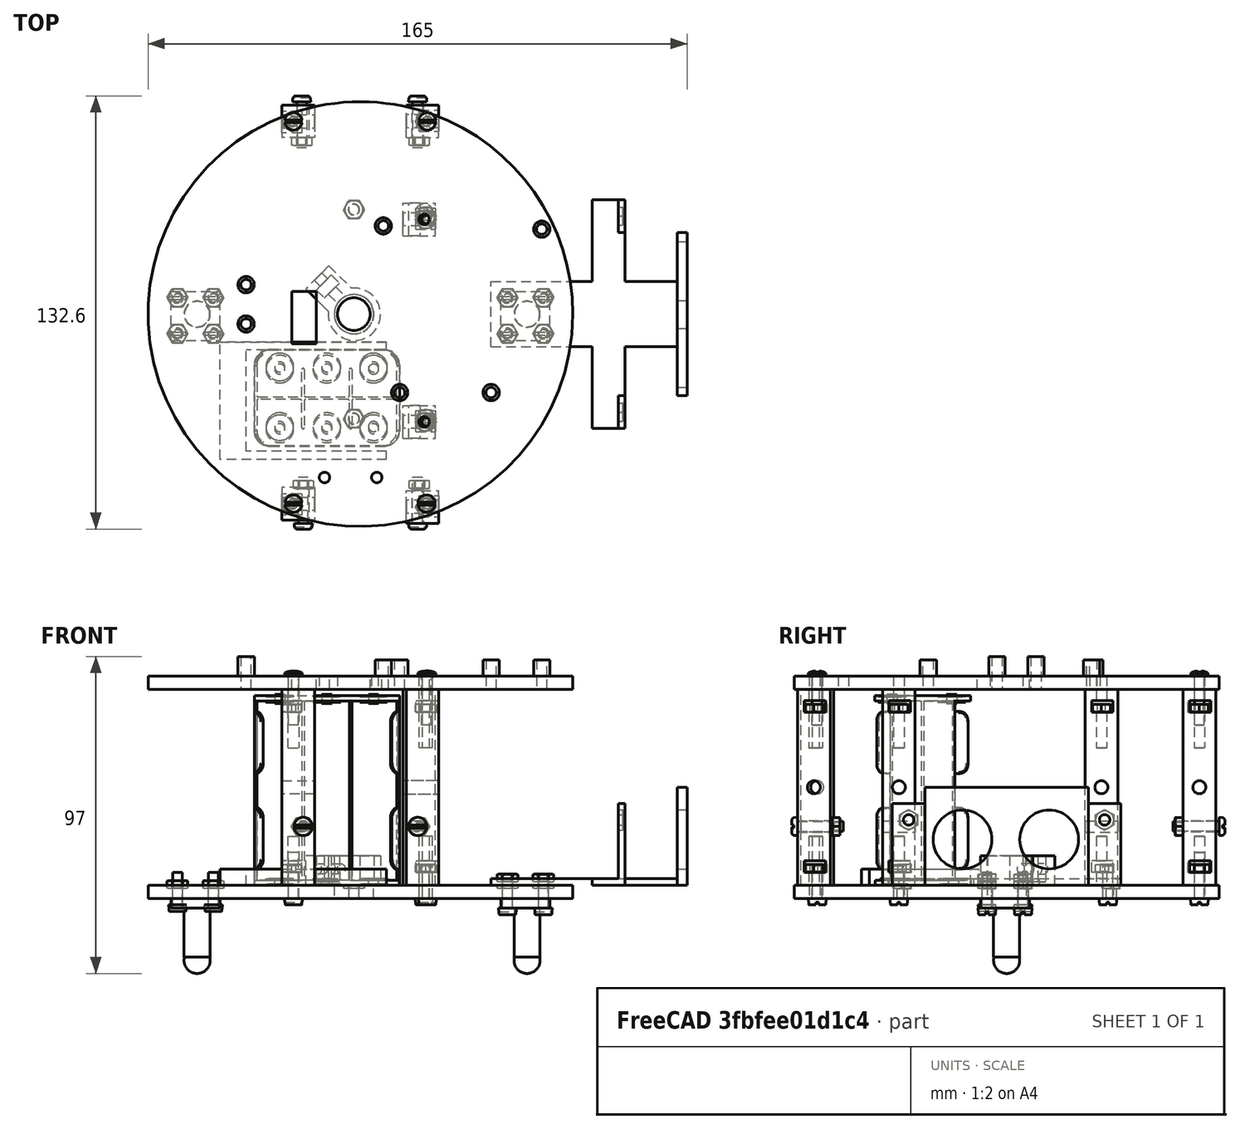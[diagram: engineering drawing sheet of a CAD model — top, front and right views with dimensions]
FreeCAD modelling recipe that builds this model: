
FCSTD DOCUMENT  (FreeCAD 0.21R33668 +26 (Git))
Label: ANIMAMOTORES
License: All rights reserved
LicenseURL: https://en.wikipedia.org/wiki/All_rights_reserved
objects: Part::FeaturePython×46, App::DocumentObjectGroupPython×21, Part::MultiFuse×14, Part::Feature×12, Mesh::Feature×2
note: 72 computed .brp shape members not serialized (recipe doc carries the construction recipe); baked Part::Feature solids carry a one-line shape summary decoded from their .brp

FEATURE [Part::Feature] Cut009_solid  label="ballCSensor"
  Placement = pos=(0,0,20) rot=(0,0,1;0rad)
  shape: bbox 15 x 15 x 23 mm, 13 faces (baked)
FEATURE [Part::Feature] Fusion060_solid  label="plataformaInferior (Solid)"
  Placement = pos=(0,0,20) rot=(0,0,1;0rad)
  shape: bbox 130 x 130 x 13 mm, 195 faces (baked)
FEATURE [Part::FeaturePython] Nut  label="M3-Tuerca"  # Fasteners workbench fastener (typed FeaturePython)
  Placement = pos=(41,5,8) rot=(0,0,1;0rad)
  diameter = 4
  invert = false
  leftHanded = false
  matchOuter = false
  offset = 0
  thread = false
  type = 22
FEATURE [Part::FeaturePython] Nut001  label="M3-Tuerca004"  # Fasteners workbench fastener (typed FeaturePython)
  Placement = pos=(52,5,8) rot=(0,0,1;0rad)
  diameter = 4
  invert = false
  leftHanded = false
  matchOuter = false
  offset = 0
  thread = false
  type = 22
FEATURE [Part::FeaturePython] Nut002  label="M3-Tuerca006"  # Fasteners workbench fastener (typed FeaturePython)
  Placement = pos=(52,-6,8) rot=(0,0,1;0rad)
  diameter = 4
  invert = false
  leftHanded = false
  matchOuter = false
  offset = 0
  thread = false
  type = 22
FEATURE [Part::FeaturePython] Nut003  label="M3-Tuerca005"  # Fasteners workbench fastener (typed FeaturePython)
  Placement = pos=(41,-6,8) rot=(0,0,1;0rad)
  diameter = 4
  invert = false
  leftHanded = false
  matchOuter = false
  offset = 0
  thread = false
  type = 22
FEATURE [Part::MultiFuse] Fusion  label="tuercasBallCSensor"
  Placement = pos=(0,0,2) rot=(0,0,1;0rad)
  Shapes = -> [Nut,Nut001,Nut002,Nut003]
FEATURE [Part::FeaturePython] Nut004  label="M3-Tuerca007"  # Fasteners workbench fastener (typed FeaturePython)
  Placement = pos=(41,5,8) rot=(0,0,1;0rad)
  diameter = 4
  invert = false
  leftHanded = false
  matchOuter = false
  offset = 0
  thread = false
  type = 22
FEATURE [Part::FeaturePython] Nut005  label="M3-Tuerca008"  # Fasteners workbench fastener (typed FeaturePython)
  Placement = pos=(52,5,8) rot=(0,0,1;0rad)
  diameter = 4
  invert = false
  leftHanded = false
  matchOuter = false
  offset = 0
  thread = false
  type = 22
FEATURE [Part::FeaturePython] Nut006  label="M3-Tuerca009"  # Fasteners workbench fastener (typed FeaturePython)
  Placement = pos=(52,-6,8) rot=(0,0,1;0rad)
  diameter = 4
  invert = false
  leftHanded = false
  matchOuter = false
  offset = 0
  thread = false
  type = 22
FEATURE [Part::FeaturePython] Nut007  label="M3-Tuerca010"  # Fasteners workbench fastener (typed FeaturePython)
  Placement = pos=(41,-6,8) rot=(0,0,1;0rad)
  diameter = 4
  invert = false
  leftHanded = false
  matchOuter = false
  offset = 0
  thread = false
  type = 22
FEATURE [Part::MultiFuse] Fusion001  label="tuercasBallCLibre"
  Placement = pos=(-101,0,0) rot=(0,0,1;0rad)
  Shapes = -> [Nut004,Nut005,Nut006,Nut007]
FEATURE [Part::Feature] Cut009_solid001  label="ballCLibre"
  Placement = pos=(-101,0,20) rot=(0,0,1;0rad)
  shape: bbox 15 x 15 x 23 mm, 13 faces (baked)
FEATURE [Part::Feature] Cut_solid  label="soporteSensores (Solid)"
  Placement = pos=(15,0,20) rot=(0,0,1;0rad)
  shape: bbox 60 x 70 x 30 mm, 144 faces (baked)
FEATURE [Part::FeaturePython] Screw  label="M3x10-Tornillo"  # Fasteners workbench fastener (typed FeaturePython)
  Placement = pos=(-60,5,3) rot=(1,0,0;3.14159rad)
  diameter = 4
  invert = false
  leftHanded = false
  length = 4
  lengthCustom = 10
  matchOuter = false
  offset = 0
  thread = false
  type = 30
FEATURE [Part::FeaturePython] Screw001  label="M3x10-Tornillo001"  # Fasteners workbench fastener (typed FeaturePython)
  Placement = pos=(-60,-6,3) rot=(1,0,0;3.14159rad)
  diameter = 4
  invert = false
  leftHanded = false
  length = 4
  lengthCustom = 10
  matchOuter = false
  offset = 0
  thread = false
  type = 30
FEATURE [Part::FeaturePython] Screw002  label="M3x10-Tornillo002"  # Fasteners workbench fastener (typed FeaturePython)
  Placement = pos=(-49,-6,3) rot=(1,0,0;3.14159rad)
  diameter = 4
  invert = false
  leftHanded = false
  length = 4
  lengthCustom = 10
  matchOuter = false
  offset = 0
  thread = false
  type = 30
FEATURE [Part::FeaturePython] Screw003  label="M3x10-Tornillo003"  # Fasteners workbench fastener (typed FeaturePython)
  Placement = pos=(-49,5,3) rot=(1,0,0;3.14159rad)
  diameter = 4
  invert = false
  leftHanded = false
  length = 4
  lengthCustom = 10
  matchOuter = false
  offset = 0
  thread = false
  type = 30
FEATURE [Part::MultiFuse] Fusion002  label="tornillosBallClibre"
  Shapes = -> [Screw,Screw001,Screw002,Screw003]
FEATURE [Part::FeaturePython] Screw004  label="M3x10-Tornillo004"  # Fasteners workbench fastener (typed FeaturePython)
  Placement = pos=(-60,5,3) rot=(1,0,0;3.14159rad)
  diameter = 4
  invert = false
  leftHanded = false
  length = 4
  lengthCustom = 10
  matchOuter = false
  offset = 0
  thread = false
  type = 30
FEATURE [Part::FeaturePython] Screw005  label="M3x10-Tornillo005"  # Fasteners workbench fastener (typed FeaturePython)
  Placement = pos=(-60,-6,3) rot=(1,0,0;3.14159rad)
  diameter = 4
  invert = false
  leftHanded = false
  length = 4
  lengthCustom = 10
  matchOuter = false
  offset = 0
  thread = false
  type = 30
FEATURE [Part::FeaturePython] Screw006  label="M3x10-Tornillo006"  # Fasteners workbench fastener (typed FeaturePython)
  Placement = pos=(-49,-6,3) rot=(1,0,0;3.14159rad)
  diameter = 4
  invert = false
  leftHanded = false
  length = 4
  lengthCustom = 10
  matchOuter = false
  offset = 0
  thread = false
  type = 30
FEATURE [Part::FeaturePython] Screw007  label="M3x10-Tornillo007"  # Fasteners workbench fastener (typed FeaturePython)
  Placement = pos=(-49,5,3) rot=(1,0,0;3.14159rad)
  diameter = 4
  invert = false
  leftHanded = false
  length = 4
  lengthCustom = 10
  matchOuter = false
  offset = 0
  thread = false
  type = 30
FEATURE [Part::MultiFuse] Fusion003  label="tornillosBallCSensor"
  Placement = pos=(101,0,-1) rot=(0,0,1;0rad)
  Shapes = -> [Screw004,Screw005,Screw006,Screw007]
FEATURE [App::DocumentObjectGroupPython] SimpleGroup  # scripted group (container) (typed FeaturePython)
  AnimationStepTime = 0
  AnimationSteps = 20
  Distance = 19
  Revolutions = 0
  dir_vectors = (1) [(0,0,1)]
  rot_centers = (1) [(-54.5,-0.5,-14)]
  rot_vectors = (1) [(0,0,1)]
FEATURE [App::DocumentObjectGroupPython] SimpleGroup003  # scripted group (container) (typed FeaturePython)
  AnimationStepTime = 0
  AnimationSteps = 20
  Distance = 20
  Revolutions = 0
  dir_vectors = (1) [(0,0,-1)]
  rot_centers = (1) [(-60,-6,26)]
  rot_vectors = (1) [(0,0,-1)]
FEATURE [App::DocumentObjectGroupPython] SimpleGroup004  # scripted group (container) (typed FeaturePython)
  AnimationStepTime = 0
  AnimationSteps = 20
  Distance = 40
  Revolutions = 0
  dir_vectors = (1) [(0,1.22465e-16,1)]
  rot_centers = (1) [(-60,5,-27)]
  rot_vectors = (1) [(0,1.22465e-16,1)]
FEATURE [App::DocumentObjectGroupPython] SimpleGroup005  # scripted group (container) (typed FeaturePython)
  AnimationStepTime = 0
  AnimationSteps = 20
  Distance = 19
  Revolutions = 0
  dir_vectors = (1) [(0,0,1)]
  rot_centers = (1) [(46.5,-0.5,-14)]
  rot_vectors = (1) [(0,0,1)]
FEATURE [Part::Feature] Part__Feature  label="6 x AAA Holder"
  Placement = pos=(-100,212,67) rot=(0.57735,0.57735,-0.57735;2.0944rad)
  shape: bbox 45.01 x 29.59 x 58.41 mm, 300 faces, 8 solids (baked)
FEATURE [App::DocumentObjectGroupPython] SimpleGroup006  # scripted group (container) (typed FeaturePython)
  AnimationStepTime = 0
  AnimationSteps = 20
  Distance = 100
  Revolutions = 0
  dir_vectors = (1) [(-1,-6.69631e-16,-2.22045e-16)]
  rot_centers = (1) [(13.5,-25.9132,38.8088)]
  rot_vectors = (1) [(-1,-6.69631e-16,-2.22045e-16)]
FEATURE [App::DocumentObjectGroupPython] SimpleGroup007  # scripted group (container) (typed FeaturePython)
  AnimationStepTime = 0
  AnimationSteps = 20
  Distance = 15
  Revolutions = 0
  dir_vectors = (1) [(0,0,-1)]
  rot_centers = (1) [(72,-3.55271e-16,24)]
  rot_vectors = (1) [(0,0,-1)]
FEATURE [App::DocumentObjectGroupPython] SimpleGroup008  # scripted group (container) (typed FeaturePython)
  AnimationStepTime = 0
  AnimationSteps = 20
  Distance = 18
  Revolutions = 0
  dir_vectors = (1) [(0,0,-1)]
  rot_centers = (1) [(52,-6,28)]
  rot_vectors = (1) [(0,0,-1)]
FEATURE [App::DocumentObjectGroupPython] SimpleGroup009  # scripted group (container) (typed FeaturePython)
  AnimationStepTime = 0
  AnimationSteps = 20
  Distance = 39
  Revolutions = 0
  dir_vectors = (1) [(0,0,1)]
  rot_centers = (1) [(52,-6,-27)]
  rot_vectors = (1) [(0,0,1)]
FEATURE [Part::Feature] Cut_solid006  label="columna (Solid)004"
  Placement = pos=(0,-21,0) rot=(0,0,1;0rad)
  shape: bbox 10 x 10 x 60 mm, 24 faces (baked)
FEATURE [Part::Feature] Cut_solid004  label="columna (Solid)002"
  Placement = pos=(-8,21,0) rot=(0,0,1;3.14159rad)
  shape: bbox 10 x 10 x 60 mm, 24 faces (baked)
FEATURE [Part::Feature] Cut_solid007  label="columna (Solid)005"
  Placement = pos=(-8,-96,0) rot=(0,0,1;3.14159rad)
  shape: bbox 10 x 10 x 60 mm, 24 faces (baked)
FEATURE [Part::Feature] Cut_solid003  label="columna (Solid)001"
  Placement = pos=(-1,67,0) rot=(0,0,1;0rad)
  shape: bbox 10 x 10 x 60 mm, 24 faces (baked)
FEATURE [Part::Feature] Cut_solid005  label="columna (Solid)003"
  Placement = pos=(0,97,0) rot=(0,0,1;0rad)
  shape: bbox 10 x 10 x 60 mm, 24 faces (baked)
FEATURE [Part::FeaturePython] Screw008  label="M3x10-Tornillo008"  # Fasteners workbench fastener (typed FeaturePython)
  Placement = pos=(-24.5,-58,5) rot=(1,0,0;3.14159rad)
  diameter = 4
  invert = false
  leftHanded = false
  length = 4
  lengthCustom = 10
  matchOuter = false
  offset = 0
  thread = false
  type = 30
FEATURE [Part::FeaturePython] Screw009  label="M3x10-Tornillo009"  # Fasteners workbench fastener (typed FeaturePython)
  Placement = pos=(16.5,-58,5) rot=(1,0,0;3.14159rad)
  diameter = 4
  invert = false
  leftHanded = false
  length = 4
  lengthCustom = 10
  matchOuter = false
  offset = 0
  thread = false
  type = 30
FEATURE [Part::FeaturePython] Screw010  label="M3x10-Tornillo010"  # Fasteners workbench fastener (typed FeaturePython)
  Placement = pos=(15.5,-33,5) rot=(1,0,0;3.14159rad)
  diameter = 4
  invert = false
  leftHanded = false
  length = 4
  lengthCustom = 10
  matchOuter = false
  offset = 0
  thread = false
  type = 30
FEATURE [Part::FeaturePython] Screw011  label="M3x10-Tornillo011"  # Fasteners workbench fastener (typed FeaturePython)
  Placement = pos=(15.5,31,5) rot=(1,0,0;3.14159rad)
  diameter = 4
  invert = false
  leftHanded = false
  length = 4
  lengthCustom = 10
  matchOuter = false
  offset = 0
  thread = false
  type = 30
FEATURE [Part::FeaturePython] Screw012  label="M3x10-Tornillo012"  # Fasteners workbench fastener (typed FeaturePython)
  Placement = pos=(16.5,59,5) rot=(1,0,0;3.14159rad)
  diameter = 4
  invert = false
  leftHanded = false
  length = 4
  lengthCustom = 10
  matchOuter = false
  offset = 0
  thread = false
  type = 30
FEATURE [Part::FeaturePython] Screw013  label="M3x14-Tornillo"  # Fasteners workbench fastener (typed FeaturePython)
  Placement = pos=(-24.5,59,5) rot=(1,0,0;3.14159rad)
  diameter = 4
  invert = false
  leftHanded = false
  length = 6
  lengthCustom = 14
  matchOuter = false
  offset = 0
  thread = false
  type = 30
FEATURE [Part::Feature] Cut_solid002  label="columna (Solid)"
  Placement = pos=(-1,5,0) rot=(0,0,1;0rad)
  shape: bbox 10 x 10 x 60 mm, 24 faces (baked)
FEATURE [Part::MultiFuse] Fusion004  label="columnas"
  Placement = pos=(0,0,20) rot=(0,0,1;0rad)
  Shapes = -> [Cut_solid006,Cut_solid004,Cut_solid007,Cut_solid003,Cut_solid005,Cut_solid002]
FEATURE [Part::MultiFuse] Fusion005  label="tornillosAbajo"
  Shapes = -> [Screw008,Screw009,Screw010,Screw011,Screw012,Screw013]
FEATURE [Part::FeaturePython] Nut008  label="M3-Tuerca011"  # Fasteners workbench fastener (typed FeaturePython)
  Placement = pos=(16,30,23) rot=(0,0,1;0rad)
  diameter = 4
  invert = false
  leftHanded = false
  matchOuter = false
  offset = 0
  thread = false
  type = 22
FEATURE [Part::FeaturePython] Nut009  label="M3-Tuerca012"  # Fasteners workbench fastener (typed FeaturePython)
  Placement = pos=(16,-32,23) rot=(0,0,1;0rad)
  diameter = 4
  invert = false
  leftHanded = false
  matchOuter = false
  offset = 0
  thread = false
  type = 22
FEATURE [Part::FeaturePython] Nut010  label="M3-Tuerca013"  # Fasteners workbench fastener (typed FeaturePython)
  Placement = pos=(16,-59,23) rot=(0,0,1;0rad)
  diameter = 4
  invert = false
  leftHanded = false
  matchOuter = false
  offset = 0
  thread = false
  type = 22
FEATURE [Part::FeaturePython] Nut011  label="M3-Tuerca014"  # Fasteners workbench fastener (typed FeaturePython)
  Placement = pos=(16,-59,72) rot=(0,0,1;0rad)
  diameter = 4
  invert = false
  leftHanded = false
  matchOuter = false
  offset = 0
  thread = false
  type = 22
FEATURE [Part::FeaturePython] Nut012  label="M3-Tuerca015"  # Fasteners workbench fastener (typed FeaturePython)
  Placement = pos=(16,-33,72) rot=(0,0,1;0rad)
  diameter = 4
  invert = false
  leftHanded = false
  matchOuter = false
  offset = 0
  thread = false
  type = 22
FEATURE [Part::FeaturePython] Nut013  label="M3-Tuerca016"  # Fasteners workbench fastener (typed FeaturePython)
  Placement = pos=(16,29,72) rot=(0,0,1;0rad)
  diameter = 4
  invert = false
  leftHanded = false
  matchOuter = false
  offset = 0
  thread = false
  type = 22
FEATURE [Part::FeaturePython] Nut014  label="M3-Tuerca017"  # Fasteners workbench fastener (typed FeaturePython)
  Placement = pos=(16,59,72) rot=(0,0,1;0rad)
  diameter = 4
  invert = false
  leftHanded = false
  matchOuter = false
  offset = 0
  thread = false
  type = 22
FEATURE [Part::FeaturePython] Nut015  label="M3-Tuerca018"  # Fasteners workbench fastener (typed FeaturePython)
  Placement = pos=(16,59,23) rot=(0,0,1;0.523599rad)
  diameter = 4
  invert = false
  leftHanded = false
  matchOuter = false
  offset = 0
  thread = false
  type = 22
FEATURE [Part::MultiFuse] Fusion006  label="tuercasDelante"
  Placement = pos=(0,0,-10) rot=(0,0,1;0rad)
  Shapes = -> [Nut015,Nut008,Nut009,Nut010,Nut011,Nut012,Nut013,Nut014]
FEATURE [App::DocumentObjectGroupPython] SimpleGroup010  # scripted group (container) (typed FeaturePython)
  AnimationStepTime = 0
  AnimationSteps = 20
  Distance = 20
  Revolutions = 0
  dir_vectors = (1) [(-1,5.55112e-16,0)]
  rot_centers = (1) [(38.25,59,24.2)]
  rot_vectors = (1) [(-1,5.55112e-16,0)]
FEATURE [Part::FeaturePython] Nut016  label="M3-Tuerca021"  # Fasteners workbench fastener (typed FeaturePython)
  Placement = pos=(-25,59,23) rot=(0,0,1;0.523599rad)
  diameter = 4
  invert = false
  leftHanded = false
  matchOuter = false
  offset = 0
  thread = false
  type = 22
FEATURE [Part::FeaturePython] Nut017  label="M3-Tuerca022"  # Fasteners workbench fastener (typed FeaturePython)
  Placement = pos=(-25,59,72) rot=(0,0,1;0.523599rad)
  diameter = 4
  invert = false
  leftHanded = false
  matchOuter = false
  offset = 0
  thread = false
  type = 22
FEATURE [Part::FeaturePython] Nut018  label="M3-Tuerca023"  # Fasteners workbench fastener (typed FeaturePython)
  Placement = pos=(-25,-58,72) rot=(0,0,1;0.523599rad)
  diameter = 4
  invert = false
  leftHanded = false
  matchOuter = false
  offset = 0
  thread = false
  type = 22
FEATURE [Part::FeaturePython] Nut019  label="M3-Tuerca024"  # Fasteners workbench fastener (typed FeaturePython)
  Placement = pos=(-25,-58,23) rot=(0,0,1;0.523599rad)
  diameter = 4
  invert = false
  leftHanded = false
  matchOuter = false
  offset = 0
  thread = false
  type = 22
FEATURE [Part::MultiFuse] Fusion007  label="tuercasAtras"
  Placement = pos=(0,0,-10) rot=(0,0,1;0rad)
  Shapes = -> [Nut019,Nut016,Nut017,Nut018]
FEATURE [App::DocumentObjectGroupPython] SimpleGroup011  # scripted group (container) (typed FeaturePython)
  AnimationStepTime = 0
  AnimationSteps = 20
  Distance = 20
  Revolutions = 0
  dir_vectors = (1) [(1,-1.66533e-16,0)]
  rot_centers = (1) [(-42.25,-58,73.2)]
  rot_vectors = (1) [(1,-1.66533e-16,0)]
FEATURE [App::DocumentObjectGroupPython] SimpleGroup012  # scripted group (container) (typed FeaturePython)
  AnimationStepTime = 0
  AnimationSteps = 20
  Distance = -10
  Revolutions = 0
  dir_vectors = (3) [(0,0,1),(0,0,1),(0,0,1)]
  rot_centers = (3) [(-2.75414,1.04693,9),(-2.75414,1.04693,9),(-2.75414,1.04693,9)]
  rot_vectors = (3) [(0,0,1),(0,0,1),(0,0,1)]
FEATURE [App::DocumentObjectGroupPython] SimpleGroup013  # scripted group (container) (typed FeaturePython)
  AnimationStepTime = 0
  AnimationSteps = 20
  Distance = -20
  Revolutions = 0
  dir_vectors = (1) [(0,0,-1)]
  rot_centers = (1) [(-4.00424,0.00296236,5)]
  rot_vectors = (1) [(0,0,-1)]
FEATURE [Mesh::Feature] _8BYJ_48_v007  label="28BYJ-48_v007"
  Placement = pos=(-8.5,-31,24.5) rot=(0,0,1;3.14159rad)
FEATURE [Mesh::Feature] _8BYJ_48_v6  label="28BYJ-48_v6"
  Placement = pos=(0.5,32,25) rot=(0,0,1;0rad)
FEATURE [Part::FeaturePython] Screw014  label="M3x14-Tornillo006"  # Fasteners workbench fastener (typed FeaturePython)
  Placement = pos=(-21.5,-64,27) rot=(1,0,0;1.5708rad)
  diameter = 4
  invert = false
  leftHanded = false
  length = 5
  lengthCustom = 14
  matchOuter = false
  offset = 0
  thread = false
  type = 36
FEATURE [Part::FeaturePython] Screw015  label="M3x14-Tornillo007"  # Fasteners workbench fastener (typed FeaturePython)
  Placement = pos=(13.5,-64,27) rot=(1,0,0;1.5708rad)
  diameter = 4
  invert = false
  leftHanded = false
  length = 5
  lengthCustom = 14
  matchOuter = false
  offset = 0
  thread = false
  type = 36
FEATURE [Part::FeaturePython] Screw016  label="M3x14-Tornillo005"  # Fasteners workbench fastener (typed FeaturePython)
  Placement = pos=(13.5,65,27) rot=(0,0.707107,0.707107;3.14159rad)
  diameter = 4
  invert = false
  leftHanded = false
  length = 5
  lengthCustom = 14
  matchOuter = false
  offset = 0
  thread = false
  type = 36
FEATURE [Part::FeaturePython] Screw017  label="M3x14-Tornillo004"  # Fasteners workbench fastener (typed FeaturePython)
  Placement = pos=(-22,65,27) rot=(0,0.707107,0.707107;3.14159rad)
  diameter = 4
  invert = false
  leftHanded = false
  length = 5
  lengthCustom = 14
  matchOuter = false
  offset = 0
  thread = false
  type = 36
FEATURE [Part::FeaturePython] Nut020  label="M3-Tuerca025"  # Fasteners workbench fastener (typed FeaturePython)
  Placement = pos=(-22,54,27) rot=(1,0,0;1.5708rad)
  diameter = 4
  invert = false
  leftHanded = false
  matchOuter = false
  offset = 0
  thread = false
  type = 22
FEATURE [Part::FeaturePython] Nut021  label="M3-Tuerca026"  # Fasteners workbench fastener (typed FeaturePython)
  Placement = pos=(14,54,27) rot=(1,0,0;1.5708rad)
  diameter = 4
  invert = false
  leftHanded = false
  matchOuter = false
  offset = 0
  thread = false
  type = 22
FEATURE [Part::FeaturePython] Nut022  label="M3-Tuerca027"  # Fasteners workbench fastener (typed FeaturePython)
  Placement = pos=(14,-51,27) rot=(1,0,0;1.5708rad)
  diameter = 4
  invert = false
  leftHanded = false
  matchOuter = false
  offset = 0
  thread = false
  type = 22
FEATURE [Part::FeaturePython] Nut023  label="M3-Tuerca028"  # Fasteners workbench fastener (typed FeaturePython)
  Placement = pos=(-21.5,-51,27) rot=(1,0,0;1.5708rad)
  diameter = 4
  invert = false
  leftHanded = false
  matchOuter = false
  offset = 0
  thread = false
  type = 22
FEATURE [Part::MultiFuse] Fusion008  label="tornillosDerecha"
  Shapes = -> [Screw014,Screw015]
FEATURE [Part::MultiFuse] Fusion009  label="tuercasDerecha"
  Shapes = -> [Nut022,Nut023]
FEATURE [App::DocumentObjectGroupPython] SimpleGroup014  # scripted group (container) (typed FeaturePython)
  AnimationStepTime = 0
  AnimationSteps = 20
  Distance = -20
  Revolutions = 0
  dir_vectors = (1) [(0,-1,0)]
  rot_centers = (1) [(-23.023,-63,39.1844)]
  rot_vectors = (1) [(0,-1,0)]
FEATURE [App::DocumentObjectGroupPython] SimpleGroup015  # scripted group (container) (typed FeaturePython)
  AnimationStepTime = 0
  AnimationSteps = 20
  Distance = -40
  Revolutions = 0
  dir_vectors = (1) [(0,-1,0)]
  rot_centers = (1) [(-23.023,-63,39.1844)]
  rot_vectors = (1) [(0,-1,0)]
FEATURE [App::DocumentObjectGroupPython] SimpleGroup016  # scripted group (container) (typed FeaturePython)
  AnimationStepTime = 0
  AnimationSteps = 20
  Distance = -10
  Revolutions = 0
  dir_vectors = (1) [(0,1,0)]
  rot_centers = (1) [(-23.023,-53,39.1844)]
  rot_vectors = (1) [(0,1,0)]
FEATURE [Part::MultiFuse] Fusion010  label="tornillosIzquierda"
  Shapes = -> [Screw016,Screw017]
FEATURE [Part::MultiFuse] Fusion011  label="tuercasIzquierda"
  Shapes = -> [Nut020,Nut021]
FEATURE [App::DocumentObjectGroupPython] SimpleGroup017  # scripted group (container) (typed FeaturePython)
  AnimationStepTime = 0
  AnimationSteps = 20
  Distance = -20
  Revolutions = 0
  dir_vectors = (1) [(0,1,0)]
  rot_centers = (1) [(-23.023,64,49.1844)]
  rot_vectors = (1) [(0,1,0)]
FEATURE [App::DocumentObjectGroupPython] SimpleGroup018  # scripted group (container) (typed FeaturePython)
  AnimationStepTime = 0
  AnimationSteps = 20
  Distance = -40
  Revolutions = 0
  dir_vectors = (1) [(0,1,0)]
  rot_centers = (1) [(-23.023,64,39.1844)]
  rot_vectors = (1) [(0,1,0)]
FEATURE [App::DocumentObjectGroupPython] SimpleGroup019  # scripted group (container) (typed FeaturePython)
  AnimationStepTime = 0
  AnimationSteps = 20
  Distance = 10
  Revolutions = 0
  dir_vectors = (1) [(0,1,0)]
  rot_centers = (1) [(-23.023,64,39.1844)]
  rot_vectors = (1) [(0,1,0)]
FEATURE [Part::Feature] Cut_solid008  label="plataformaSuperior (Solid)"
  Placement = pos=(0,0,20) rot=(0,0,1;0rad)
  shape: bbox 130 x 130 x 10 mm, 42 faces (baked)
FEATURE [Part::FeaturePython] Screw018  label="M3x16-Tornillo"  # Fasteners workbench fastener (typed FeaturePython)
  Placement = pos=(16.5,59,74) rot=(0,0,1;0rad)
  diameter = 4
  invert = false
  leftHanded = false
  length = 6
  lengthCustom = 16
  matchOuter = false
  offset = 0
  thread = false
  type = 38
FEATURE [Part::FeaturePython] Screw019  label="M3x16-Tornillo001"  # Fasteners workbench fastener (typed FeaturePython)
  Placement = pos=(-24.5,59,74) rot=(0,0,1;0rad)
  diameter = 4
  invert = false
  leftHanded = false
  length = 6
  lengthCustom = 16
  matchOuter = false
  offset = 0
  thread = false
  type = 38
FEATURE [Part::FeaturePython] Screw020  label="M3x16-Tornillo002"  # Fasteners workbench fastener (typed FeaturePython)
  Placement = pos=(-24.5,-58,74) rot=(0,0,1;0rad)
  diameter = 4
  invert = false
  leftHanded = false
  length = 6
  lengthCustom = 16
  matchOuter = false
  offset = 0
  thread = false
  type = 38
FEATURE [Part::FeaturePython] Screw021  label="M3x16-Tornillo003"  # Fasteners workbench fastener (typed FeaturePython)
  Placement = pos=(16.2,-58,74) rot=(0,0,1;0rad)
  diameter = 4
  invert = false
  leftHanded = false
  length = 6
  lengthCustom = 16
  matchOuter = false
  offset = 0
  thread = false
  type = 38
FEATURE [Part::MultiFuse] Fusion012  label="tornillosSuperiorIzquierda"
  Shapes = -> [Screw018,Screw019]
FEATURE [Part::MultiFuse] Fusion013  label="tornillosSuperiorDerecha"
  Shapes = -> [Screw020,Screw021]
FEATURE [App::DocumentObjectGroupPython] SimpleGroup020  # scripted group (container) (typed FeaturePython)
  AnimationStepTime = 0
  AnimationSteps = 20
  Distance = -20
  Revolutions = 0
  dir_vectors = (1) [(0,0,1)]
  rot_centers = (1) [(-22.8688,-58,69)]
  rot_vectors = (1) [(0,0,1)]
FEATURE [App::DocumentObjectGroupPython] SimpleGroup021  # scripted group (container) (typed FeaturePython)
  AnimationStepTime = 0
  AnimationSteps = 20
  Distance = -40
  Revolutions = 0
  dir_vectors = (2) [(0,0,1),(0,0,1)]
  rot_centers = (2) [(-3.91562,0.0566826,73),(-3.91562,0.0566826,73)]
  rot_vectors = (2) [(0,0,1),(0,0,1)]
FEATURE [App::DocumentObjectGroupPython] ExplodedAssembly  # scripted group (container) (typed FeaturePython)
  AnimationStep = 0
  CurrentTrajectory = -1
  Group = -> [SimpleGroup,SimpleGroup003,SimpleGroup004,SimpleGroup005,SimpleGroup006,SimpleGroup007,SimpleGroup008,SimpleGroup009,SimpleGroup010,SimpleGroup011,SimpleGroup012,SimpleGroup013,SimpleGroup014,SimpleGroup015,SimpleGroup016,SimpleGroup017,SimpleGroup018,SimpleGroup019,SimpleGroup020,SimpleGroup021]
  InAnimation = false
  RemoveAllTrajectories = false
  ResetAnimation = false
